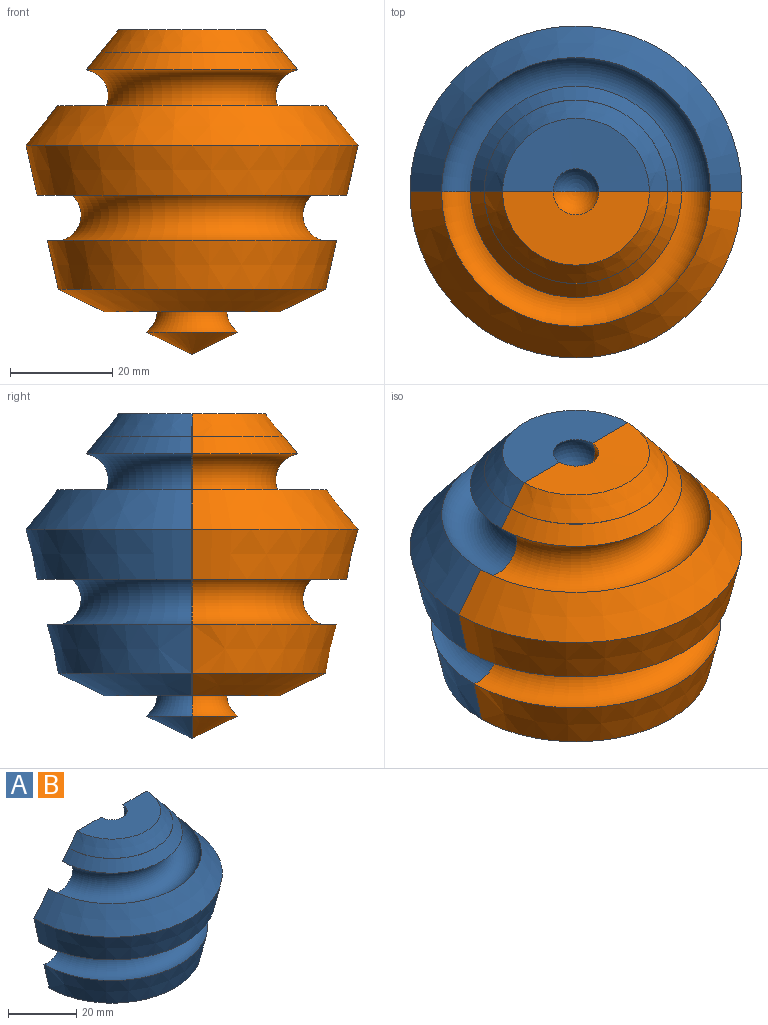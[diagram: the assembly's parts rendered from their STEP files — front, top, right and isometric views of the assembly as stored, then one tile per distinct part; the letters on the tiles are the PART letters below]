
ASSEMBLY  parts=2 mates=1
PART A: 29 faces, bbox 66x33x63.3 mm
  f0: torus R=12.98mm, axis (0,0,-1), area 2.1mm2, adj f1,f13,f14
  f1: cone r=17.92mm half-angle=38.6deg, axis (0,0,-1), area 264.9mm2, adj f0,f2,f14
  f2: torus R=21.5mm, axis (0,0,-1), area 1333.1mm2, adj f1,f3,f14
  f3: cone r=26.27mm half-angle=38.8deg, axis (0,0,-1), area 908.2mm2, adj f2,f4,f14
  f4: cone r=32.44mm half-angle=12.7deg, axis (0,0,1), area 988.5mm2, adj f3,f5,f14
  f5: torus R=26.81mm, axis (0,0,-1), area 1660.3mm2, adj f4,f6,f14
  f6: cone r=28.26mm half-angle=12.7deg, axis (0,0,1), area 841.1mm2, adj f5,f7,f14
  f7: cone r=26.11mm half-angle=64.1deg, axis (0,0,1), area 681mm2, adj f6,f8,f14
  f8: torus R=11.93mm, axis (0,0,-1), area 738.5mm2, adj f7,f9,f14
  f9: cone r=8.97mm half-angle=64.1deg, axis (0,0,1), area 140.6mm2, adj f8,f10,f14
  f10: cone r=0.12mm half-angle=64.5deg, axis (0,0,-1), area 0mm2, adj f9,f14
  f11: sphere r=5.15mm, area 124mm2, adj f12,f14
  f12: cone r=4.49mm half-angle=89.8deg, axis (0,0,1), area 291.4mm2, adj f11,f13,f14
  f13: cone r=14.34mm half-angle=38.8deg, axis (0,0,-1), area 288.8mm2, adj f0,f12,f14
  f14: plane 64.87x63.35mm, normal (0,1,0), area 2535.9mm2, adj f0,f1,f2,f3,f4,f5,f6,f7
  f15: cylinder r=1.25mm len=2.5mm, axis (0,1,0), area 19.6mm2, adj f14,f16
  f16: plane 2.5x2.5mm, normal (0,1,0), area 4.9mm2, adj f15
  f17: cylinder r=1.25mm len=2.5mm, axis (0,1,0), area 19.6mm2, adj f14,f18
  f18: plane 2.5x2.5mm, normal (0,1,0), area 4.9mm2, adj f17
  f19: cylinder r=1.25mm len=2.5mm, axis (0,1,0), area 19.6mm2, adj f14,f20
  f20: plane 2.5x2.5mm, normal (0,1,0), area 4.9mm2, adj f19
  f21: cylinder r=1.25mm len=2.5mm, axis (0,1,0), area 19.6mm2, adj f14,f22
  f22: plane 2.5x2.5mm, normal (0,1,0), area 4.9mm2, adj f21
  f23: cylinder r=1.25mm len=2.5mm, axis (0,1,0), area 19.6mm2, adj f14,f24
  f24: plane 2.5x2.5mm, normal (0,1,0), area 4.9mm2, adj f23
  f25: cylinder r=1.25mm len=2.5mm, axis (0,1,0), area 19.6mm2, adj f14,f26
  f26: plane 2.5x2.5mm, normal (0,1,0), area 4.9mm2, adj f25
  f27: cylinder r=1.25mm len=2.5mm, axis (0,1,0), area 19.6mm2, adj f14,f28
  f28: plane 2.5x2.5mm, normal (0,1,0), area 4.9mm2, adj f27
PART B: same geometry as A
PLACE A rot(axis=(0,0,1),180deg) t=(-67.6,-7.9,14.03)mm
PLACE B t=(-67.6,-7.9,14.03)mm
MATE revolute A.f14 <-> B.f14  axis (0,-1,0) through (-67.6,-7.9,14.03)mm
